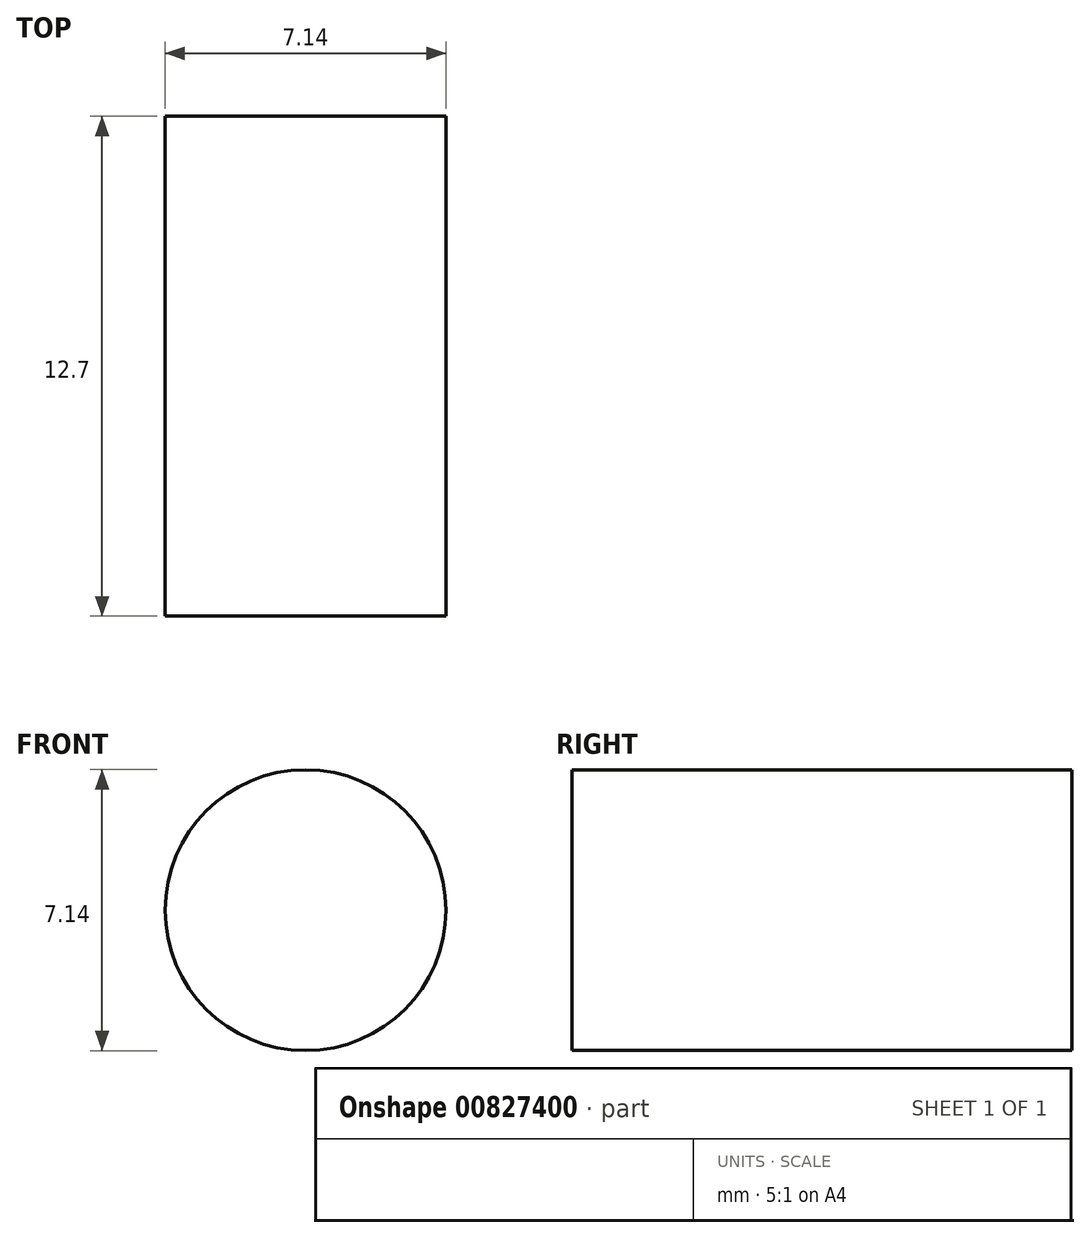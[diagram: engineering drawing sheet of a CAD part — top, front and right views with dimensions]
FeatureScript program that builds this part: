
annotation { "Feature Type Name" : "Feature", "Feature Type Description" : "" }
export const myFeature = defineFeature(function(context is Context, id is Id, definition is map)
    precondition{}
    {
        {
            var Q0;
            Q0=qCreatedBy(makeId("Front.planeOp"),FACE);
            var sketch = newSketch(context, id + "F0", { "sketchPlane" : qUnion([Q0])});
            skCircle(sketch, "E0", {"center": v(0, 0) * mm, "radius": 3.57 * mm});
            skSolve(sketch);
        }
        {
            var Q0;
            Q0 = qSketchRegion(id + "F0", true);
            extrude(context, id + "F1", {"entities" : qUnion([Q0]), "endBound" : BoundingType.SYMMETRIC, "depth" : 12.7 * mm, "offsetDistance" : 25.4 * mm});
        }
    });
